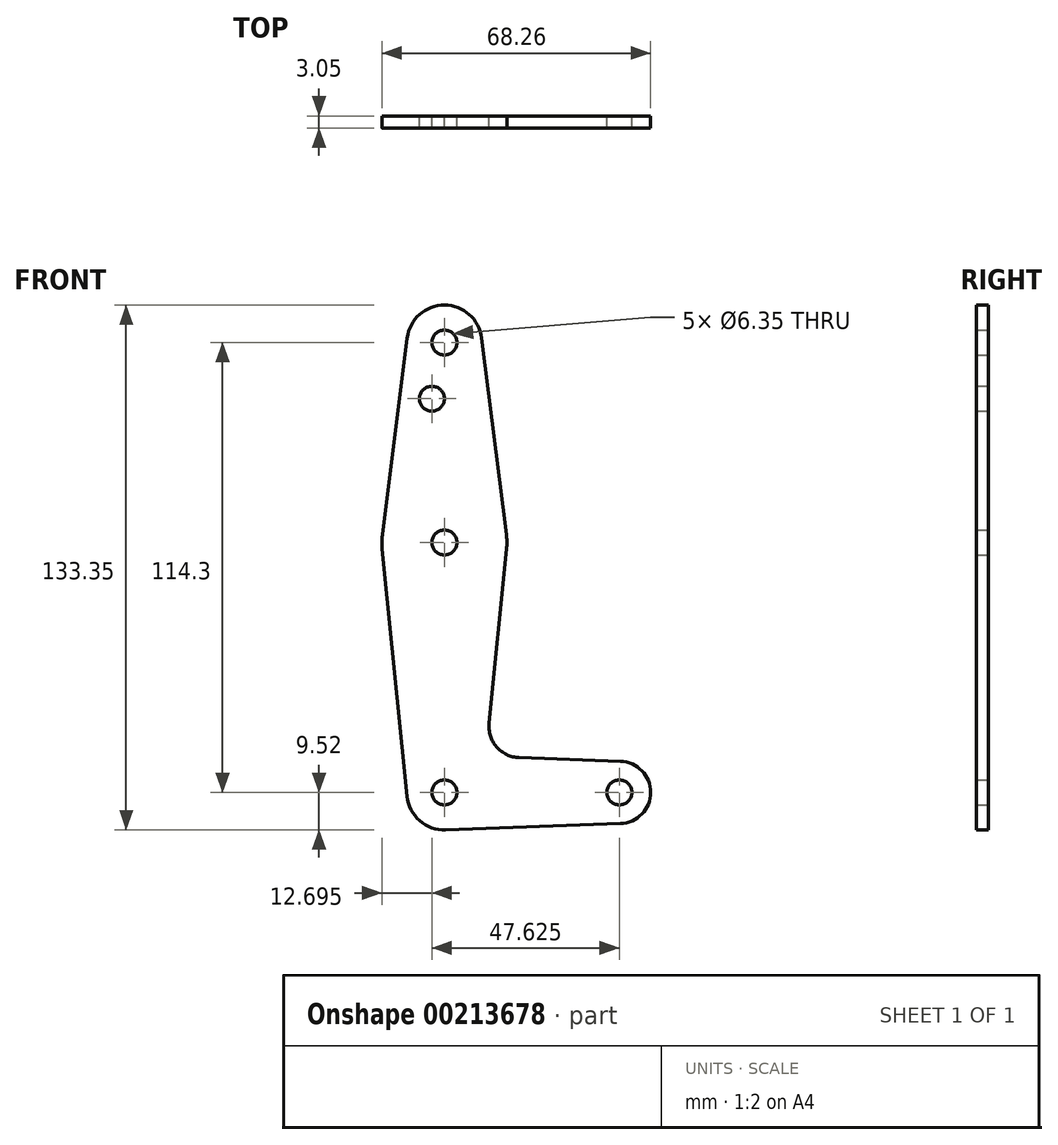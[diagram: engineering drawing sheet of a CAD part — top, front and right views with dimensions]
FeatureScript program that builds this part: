
annotation { "Feature Type Name" : "Feature", "Feature Type Description" : "" }
export const myFeature = defineFeature(function(context is Context, id is Id, definition is map)
    precondition{}
    {
        {
            var Q0;
            Q0=qCreatedBy(makeId("Front.planeOp"),FACE);
            var sketch = newSketch(context, id + "F0", { "sketchPlane" : qUnion([Q0])});
            skLineSegment(sketch, "E0", {"start": v(0, 0) * mm, "end": v(0, 114.3) * mm, "construction": true});
            skLineSegment(sketch, "E1", {"start": v(0, 0) * mm, "end": v(44.45, 0) * mm, "construction": true});
            skCircle(sketch, "E2", {"center": v(0, 114.3) * mm, "radius": 9.53 * mm});
            skCircle(sketch, "E3", {"center": v(0, 63.5) * mm, "radius": 15.88 * mm});
            skCircle(sketch, "E4", {"center": v(0, 0) * mm, "radius": 9.53 * mm});
            skCircle(sketch, "E5", {"center": v(44.45, 0) * mm, "radius": 7.94 * mm});
            skLineSegment(sketch, "E6", {"start": v(0, 63.5) * mm, "end": v(0, 0) * mm});
            skLineSegment(sketch, "E7", {"start": v(-9.45, 115.5) * mm, "end": v(-15.75, 65.48) * mm});
            skLineSegment(sketch, "E8", {"start": v(11.34, 17.6) * mm, "end": v(15.8, 61.91) * mm});
            skLineSegment(sketch, "E9", {"start": v(15.75, 65.48) * mm, "end": v(9.45, 115.5) * mm});
            skLineSegment(sketch, "E10", {"start": v(18.97, 8.85) * mm, "end": v(44.73, 7.93) * mm});
            skLineSegment(sketch, "E11", {"start": v(0.34, -9.52) * mm, "end": v(44.73, -7.93) * mm});
            skLineSegment(sketch, "E12", {"start": v(-15.8, 61.91) * mm, "end": v(-9.48, -0.95) * mm});
            skCircle(sketch, "E13", {"center": v(0, 114.3) * mm, "radius": 3.18 * mm});
            skCircle(sketch, "E14", {"center": v(0, 63.5) * mm, "radius": 3.18 * mm});
            skCircle(sketch, "E15", {"center": v(0, 0) * mm, "radius": 3.18 * mm});
            skCircle(sketch, "E16", {"center": v(44.45, 0) * mm, "radius": 3.18 * mm});
            skArc(sketch, "E17.filletArc", {"start": v(11.34, 17.6) * mm, "mid": v(13.26, 11.57) * mm, "end": v(18.97, 8.85) * mm});
            skCircle(sketch, "E18", {"center": v(-3.18, 100.03) * mm, "radius": 3.18 * mm});
            skSolve(sketch);
        }
        {
            var Q0;
            {var subQ1=sQuery(id+"F0.wireOp",EDGE,"E7");Q0=makeQuery(id+"F0.imprint","IMPRINT",FACE,{"disambiguationData":[TD([[makeQuery(id+"F0.imprint","IMPRINT",EDGE,{"derivedFrom":subQ1}),1.0]])]});}
            var Q1;
            Q1=makeQuery(id+"F0.imprint","IMPRINT",FACE,{"disambiguationData":[TD([[makeQuery(id+"F0.imprint","IMPRINT",EDGE,{"derivedFrom":sQuery(id+"F0.wireOp",EDGE,"E13")}),-1.0]])]});
            var Q2;
            Q2=makeQuery(id+"F0.imprint","IMPRINT",FACE,{"disambiguationData":[TD([[makeQuery(id+"F0.imprint","IMPRINT",EDGE,{"derivedFrom":sQuery(id+"F0.wireOp",EDGE,"E14")}),-1.0]])]});
            var Q3;
            {var subQ5=sQuery(id+"F0.wireOp",EDGE,"E8");Q3=makeQuery(id+"F0.imprint","IMPRINT",FACE,{"disambiguationData":[TD([[makeQuery(id+"F0.imprint","IMPRINT",EDGE,{"derivedFrom":subQ5}),1.0]])]});}
            var Q4;
            Q4=makeQuery(id+"F0.imprint","IMPRINT",FACE,{"disambiguationData":[TD([[makeQuery(id+"F0.imprint","IMPRINT",EDGE,{"derivedFrom":sQuery(id+"F0.wireOp",EDGE,"E15")}),-1.0]])]});
            var Q5;
            {var subQ0=sQuery(id+"F0.wireOp",EDGE,"E12");Q5=makeQuery(id+"F0.imprint","IMPRINT",FACE,{"disambiguationData":[TD([[makeQuery(id+"F0.imprint","IMPRINT",EDGE,{"derivedFrom":subQ0}),1.0]])]});}
            var Q6;
            Q6=makeQuery(id+"F0.imprint","IMPRINT",FACE,{"disambiguationData":[TD([[makeQuery(id+"F0.imprint","IMPRINT",EDGE,{"derivedFrom":sQuery(id+"F0.wireOp",EDGE,"E16")}),-1.0]])]});
            extrude(context, id + "F1", {"entities" : qUnion([Q0, Q1, Q2, Q3, Q4, Q5, Q6]), "depth" : 3.05 * mm});
        }
    });
